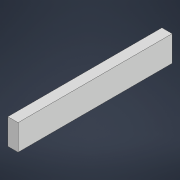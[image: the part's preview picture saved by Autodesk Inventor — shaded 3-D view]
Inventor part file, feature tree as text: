
AUTODESK INVENTOR PART (.ipt)
format: ipt  version: 2022 (Build 260153000, 153)  size: 94,720 bytes
history: native  units: mm
features: other x1, extrude x1, sketch x1
ambient origin geometry x8: Origin, YZ Plane, XZ Plane, XY Plane, X Axis, Y Axis, Z Axis, Center Point
bodies: Body1 (feature_tree)
feature tree (3):
  other  "Твердое тело1"
  extrude  "Выдавливание1"  Depth=10.0mm
  sketch  "Эскиз1"
